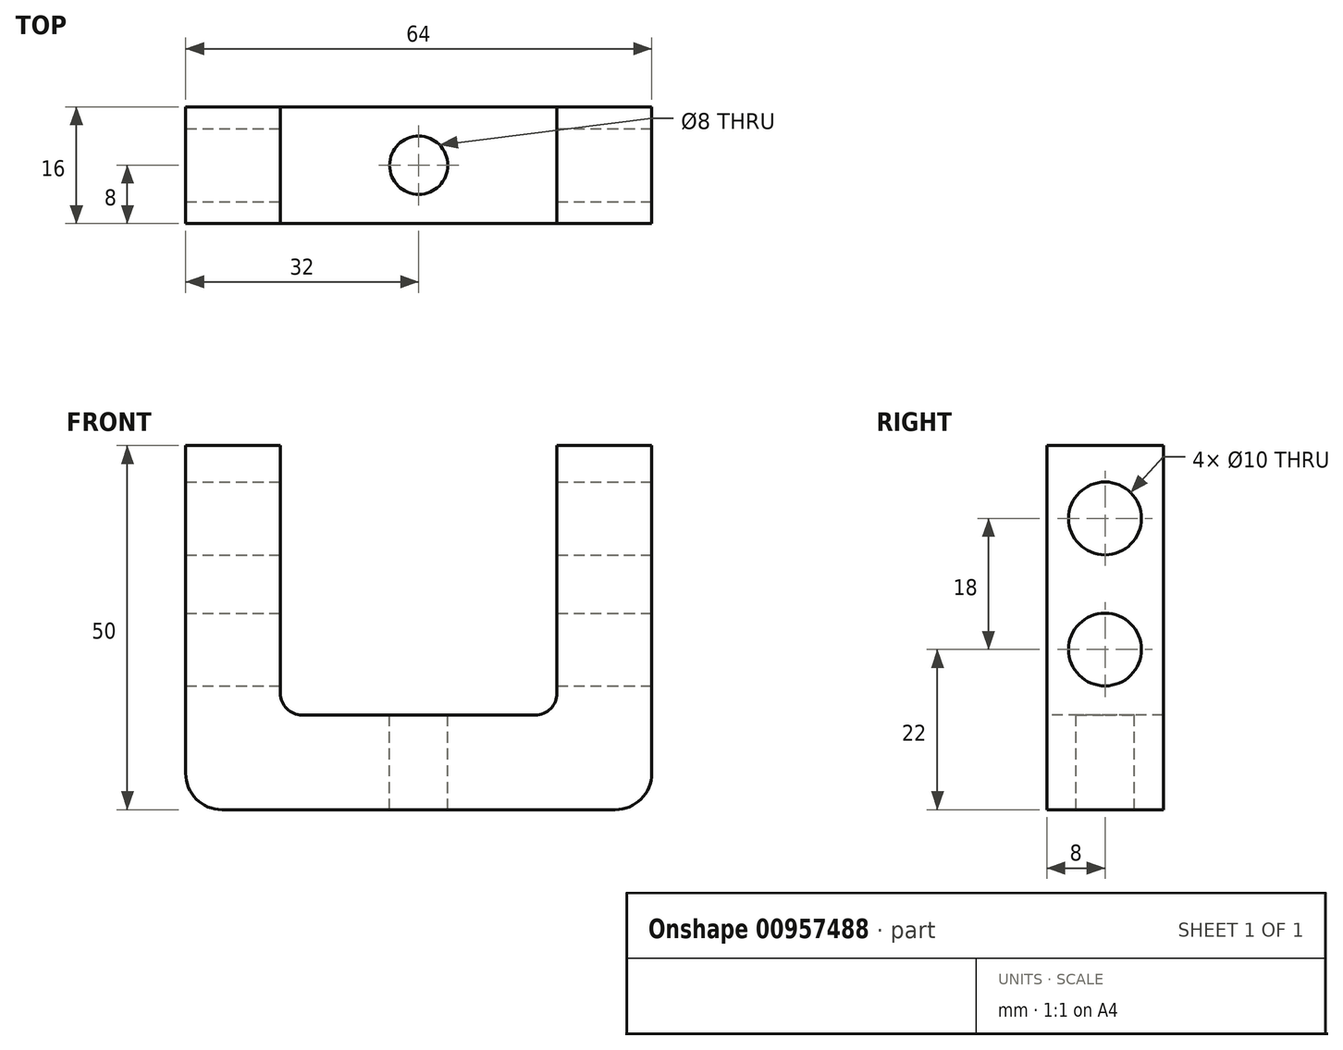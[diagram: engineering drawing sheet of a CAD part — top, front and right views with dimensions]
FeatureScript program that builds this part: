
annotation { "Feature Type Name" : "Feature", "Feature Type Description" : "" }
export const myFeature = defineFeature(function(context is Context, id is Id, definition is map)
    precondition{}
    {
        {
            var Q0;
            Q0=qCreatedBy(makeId("Front.planeOp"),FACE);
            var sketch = newSketch(context, id + "F0", { "sketchPlane" : qUnion([Q0])});
            skLineSegment(sketch, "E0", {"start": v(0, 0) * mm, "end": v(-32, 0) * mm});
            skLineSegment(sketch, "E1", {"start": v(-32, 0) * mm, "end": v(-32, 50) * mm});
            skLineSegment(sketch, "E2.0", {"start": v(-19, 13) * mm, "end": v(-19, 50) * mm});
            skLineSegment(sketch, "E3.0", {"start": v(0, 13) * mm, "end": v(-19, 13) * mm});
            skLineSegment(sketch, "E4", {"start": v(-32, 50) * mm, "end": v(-19, 50) * mm});
            skLineSegment(sketch, "E5", {"start": v(0, 0) * mm, "end": v(0, 13) * mm});
            skLineSegment(sketch, "E6", {"start": v(0, 0) * mm, "end": v(0, -16.66) * mm});
            skLineSegment(sketch, "E7.MirrorCS", {"start": v(32, 0) * mm, "end": v(32, 50) * mm});
            skLineSegment(sketch, "E8.MirrorCS", {"start": v(19, 13) * mm, "end": v(19, 50) * mm});
            skLineSegment(sketch, "E9.MirrorCS", {"start": v(0, 13) * mm, "end": v(19, 13) * mm});
            skLineSegment(sketch, "E10.MirrorCS", {"start": v(0, 0) * mm, "end": v(32, 0) * mm});
            skLineSegment(sketch, "E11.MirrorCS", {"start": v(32, 50) * mm, "end": v(19, 50) * mm});
            skPoint(sketch, "E12.orphan", {"position": v(-19, 0) * mm});
            skPoint(sketch, "E13.orphan", {"position": v(19, 0) * mm});
            skSolve(sketch);
        }
        {
            var Q0;
            Q0=makeQuery(id+"F0.imprint","IMPRINT",FACE,{"disambiguationData":[TD([[makeQuery(id+"F0.imprint","IMPRINT",EDGE,{"derivedFrom":sQuery(id+"F0.wireOp",EDGE,"E0")}),-1.0]])]});
            var Q1;
            Q1=makeQuery(id+"F0.imprint","IMPRINT",FACE,{"disambiguationData":[TD([[makeQuery(id+"F0.imprint","IMPRINT",EDGE,{"derivedFrom":sQuery(id+"F0.wireOp",EDGE,"E7.MirrorCS")}),1.0]])]});
            extrude(context, id + "F1", {"entities" : qUnion([Q0, Q1]), "oppositeDirection" : true, "depth" : 16 * mm, "offsetDistance" : 25 * mm});
        }
        {
            var Q0;
            Q0=makeQuery(id+"F1.opExtrude","SWEPT_FACE",FACE,{"disambiguationData":[OSD([sQuery(id+"F0.wireOp",EDGE,"E3.0"),sQuery(id+"F0.wireOp",EDGE,"E9.MirrorCS")])]});
            var sketch = newSketch(context, id + "F2", { "sketchPlane" : qUnion([Q0])});
            skCircle(sketch, "E14", {"center": v(0, 8) * mm, "radius": 4 * mm});
            skSolve(sketch);
        }
        {
            var Q0;
            Q0=makeQuery(id+"F2.imprint","IMPRINT",FACE,{"disambiguationData":[TD([[makeQuery(id+"F2.imprint","IMPRINT",EDGE,{"derivedFrom":sQuery(id+"F2.wireOp",EDGE,"E14")}),1.0]])]});
            var Q1;
            Q1=sQuery(id+"F2.wireOp",EDGE,"E14");
            extrude(context, id + "F3", {"entities" : qUnion([Q0]), "operationType" : NewBodyOperationType.REMOVE, "surfaceEntities" : qUnion([Q1]), "oppositeDirection" : true, "depth" : 13 * mm, "offsetDistance" : 25 * mm});
        }
        {
            var Q0;
            Q0=makeQuery(id+"F1.opExtrude","SWEPT_FACE",FACE,{"disambiguationData":[OSD([sQuery(id+"F0.wireOp",EDGE,"E7.MirrorCS")])]});
            var sketch = newSketch(context, id + "F4", { "sketchPlane" : qUnion([Q0])});
            skCircle(sketch, "E15", {"center": v(8, 40) * mm, "radius": 5 * mm});
            skPoint(sketch, "E15.centerSnap0", {"position": v(8, 50) * mm});
            skCircle(sketch, "E16", {"center": v(8, 22) * mm, "radius": 5 * mm});
            skSolve(sketch);
        }
        {
            var Q0;
            Q0=makeQuery(id+"F4.imprint","IMPRINT",FACE,{"disambiguationData":[TD([[makeQuery(id+"F4.imprint","IMPRINT",EDGE,{"derivedFrom":sQuery(id+"F4.wireOp",EDGE,"E16")}),1.0]])]});
            var Q1;
            Q1=makeQuery(id+"F4.imprint","IMPRINT",FACE,{"disambiguationData":[TD([[makeQuery(id+"F4.imprint","IMPRINT",EDGE,{"derivedFrom":sQuery(id+"F4.wireOp",EDGE,"E15")}),1.0]])]});
            var Q2;
            Q2=sQuery(id+"F4.wireOp",EDGE,"E16");
            extrude(context, id + "F5", {"entities" : qUnion([Q0, Q1]), "operationType" : NewBodyOperationType.REMOVE, "surfaceEntities" : qUnion([Q2]), "oppositeDirection" : true, "depth" : 65 * mm, "offsetDistance" : 25 * mm});
        }
        {
            var Q0;
            Q0=makeQuery(id+"F1.opExtrude","SWEPT_EDGE",EDGE,{"disambiguationData":[OSD([sQuery(id+"F0.wireOp",EDGE,"E7.MirrorCS"),sQuery(id+"F0.wireOp",EDGE,"E10.MirrorCS")])]});
            fillet(context, id + "F6", {"entities" : qUnion([Q0]), "radius" : 5 * mm, "tangentPropagation" : true, "allowEdgeOverflow" : false});
        }
        {
            var Q0;
            Q0=makeQuery(id+"F1.opExtrude","SWEPT_EDGE",EDGE,{"disambiguationData":[OSD([sQuery(id+"F0.wireOp",EDGE,"E0"),sQuery(id+"F0.wireOp",EDGE,"E1")])]});
            fillet(context, id + "F7", {"entities" : qUnion([Q0]), "radius" : 5 * mm, "tangentPropagation" : true, "allowEdgeOverflow" : false});
        }
        {
            var Q0;
            Q0=makeQuery(id+"F1.opExtrude","SWEPT_EDGE",EDGE,{"disambiguationData":[OSD([sQuery(id+"F0.wireOp",EDGE,"E2.0"),sQuery(id+"F0.wireOp",EDGE,"E3.0")])]});
            fillet(context, id + "F8", {"entities" : qUnion([Q0]), "radius" : 3 * mm, "tangentPropagation" : true, "allowEdgeOverflow" : false});
        }
        {
            var Q0;
            Q0=makeQuery(id+"F1.opExtrude","SWEPT_EDGE",EDGE,{"disambiguationData":[OSD([sQuery(id+"F0.wireOp",EDGE,"E8.MirrorCS"),sQuery(id+"F0.wireOp",EDGE,"E9.MirrorCS")])]});
            fillet(context, id + "F9", {"entities" : qUnion([Q0]), "radius" : 3 * mm, "tangentPropagation" : true, "allowEdgeOverflow" : false});
        }
    });
